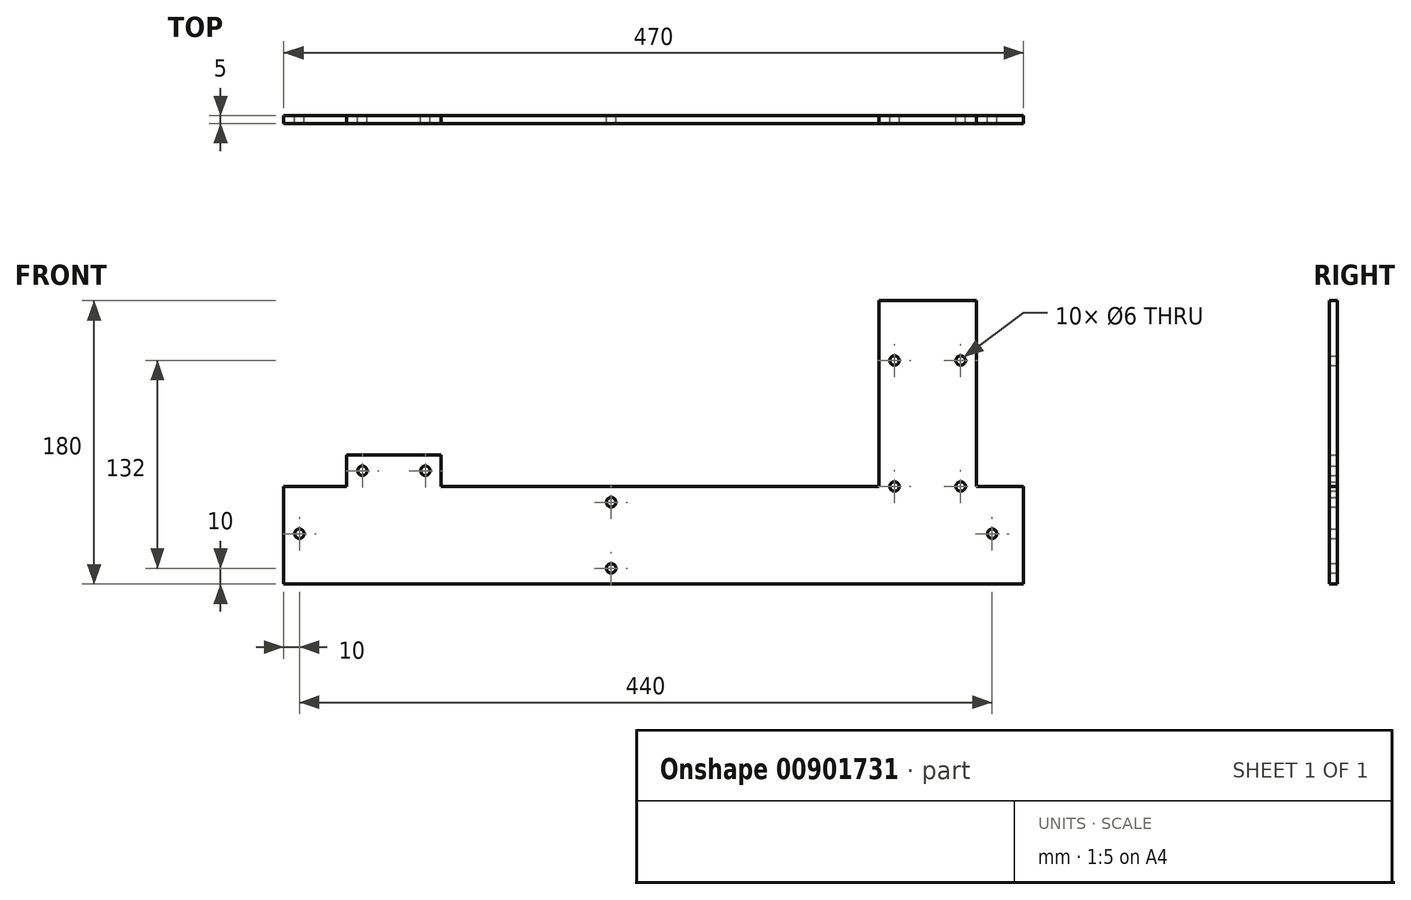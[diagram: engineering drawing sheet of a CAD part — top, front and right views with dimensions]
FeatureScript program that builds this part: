
annotation { "Feature Type Name" : "Feature", "Feature Type Description" : "" }
export const myFeature = defineFeature(function(context is Context, id is Id, definition is map)
    precondition{}
    {
        {
            var Q0;
            Q0=qCreatedBy(makeId("Front.planeOp"),FACE);
            var sketch = newSketch(context, id + "F0", { "sketchPlane" : qUnion([Q0])});
            skLineSegment(sketch, "E0", {"start": v(0, 118) * mm, "end": v(62, 118) * mm});
            skLineSegment(sketch, "E1", {"start": v(62, 118) * mm, "end": v(62, 0) * mm});
            skLineSegment(sketch, "E2", {"start": v(62, 0) * mm, "end": v(92, 0) * mm});
            skLineSegment(sketch, "E3", {"start": v(92, 0) * mm, "end": v(92, -62) * mm});
            skLineSegment(sketch, "E4", {"start": v(92, -62) * mm, "end": v(-378, -62) * mm});
            skLineSegment(sketch, "E5", {"start": v(-378, -62) * mm, "end": v(-378, 0) * mm});
            skLineSegment(sketch, "E6", {"start": v(-378, 0) * mm, "end": v(-338, 0) * mm});
            skLineSegment(sketch, "E7", {"start": v(-338, 0) * mm, "end": v(-338, 20) * mm});
            skLineSegment(sketch, "E8", {"start": v(-338, 20) * mm, "end": v(-278, 20) * mm});
            skLineSegment(sketch, "E9", {"start": v(-278, 20) * mm, "end": v(-278, 0) * mm});
            skLineSegment(sketch, "E10", {"start": v(-278, 0) * mm, "end": v(0, 0) * mm});
            skLineSegment(sketch, "E11", {"start": v(0, 0) * mm, "end": v(0, 118) * mm});
            skCircle(sketch, "E12", {"center": v(10, 80) * mm, "radius": 3 * mm});
            skCircle(sketch, "E13", {"center": v(52, 80) * mm, "radius": 3 * mm});
            skCircle(sketch, "E14", {"center": v(52, 0) * mm, "radius": 3 * mm});
            skCircle(sketch, "E15", {"center": v(10, 0) * mm, "radius": 3 * mm});
            skCircle(sketch, "E16", {"center": v(72, -30) * mm, "radius": 3 * mm});
            skCircle(sketch, "E17", {"center": v(-368, -30) * mm, "radius": 3 * mm});
            skCircle(sketch, "E18", {"center": v(-170, -10) * mm, "radius": 3 * mm});
            skCircle(sketch, "E19", {"center": v(-170, -52) * mm, "radius": 3 * mm});
            skCircle(sketch, "E20", {"center": v(-328, 10) * mm, "radius": 3 * mm});
            skCircle(sketch, "E21", {"center": v(-288, 10) * mm, "radius": 3 * mm});
            skSolve(sketch);
        }
        {
            var Q0;
            Q0=makeQuery(id+"F0.imprint","IMPRINT",FACE,{"disambiguationData":[TD([[makeQuery(id+"F0.imprint","IMPRINT",EDGE,{"derivedFrom":sQuery(id+"F0.wireOp",EDGE,"E0")}),-1.0]])]});
            extrude(context, id + "F1", {"entities" : qUnion([Q0]), "depth" : 5 * mm, "offsetDistance" : 25 * mm});
        }
    });
